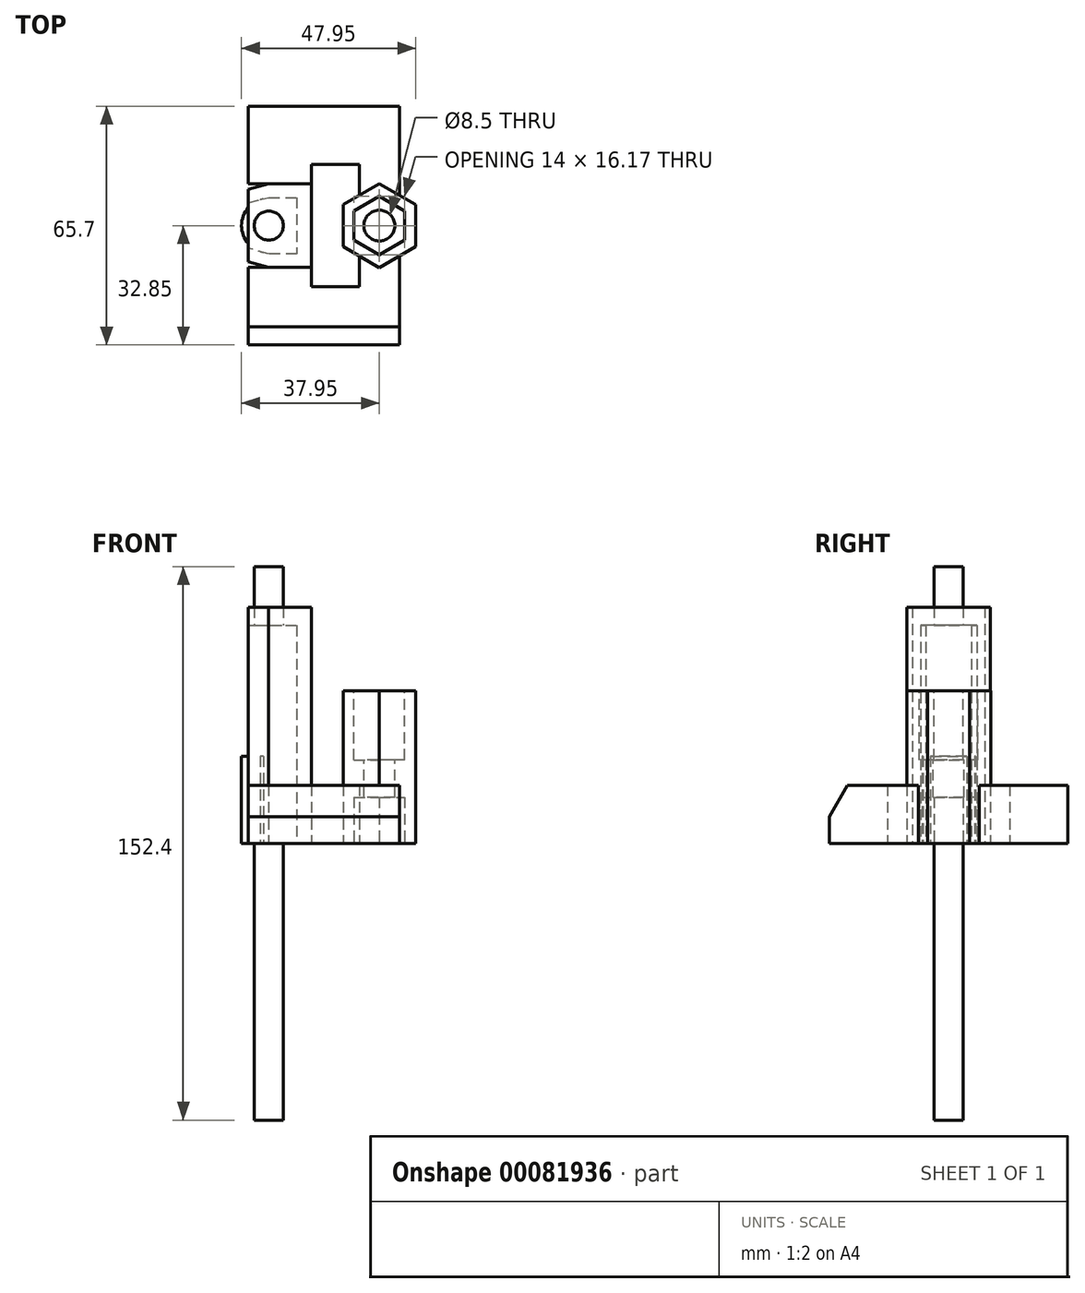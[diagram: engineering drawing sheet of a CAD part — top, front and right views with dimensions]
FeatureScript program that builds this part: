
annotation { "Feature Type Name" : "Feature", "Feature Type Description" : "" }
export const myFeature = defineFeature(function(context is Context, id is Id, definition is map)
    precondition{}
    {
        {
            var Q0;
            Q0=qCreatedBy(makeId("Top.planeOp"),FACE);
            var sketch = newSketch(context, id + "F0", { "sketchPlane" : qUnion([Q0])});
            skCircle(sketch, "E0", {"center": v(0, 0) * mm, "radius": 4 * mm});
            skSolve(sketch);
        }
        {
            var Q0;
            Q0 = qSketchRegion(id + "F0", true);
            extrude(context, id + "F1", {"entities" : qUnion([Q0]), "endBound" : BoundingType.SYMMETRIC, "depth" : 152.4 * mm});
        }
        {
            var Q0;
            Q0=qCreatedBy(makeId("Top.planeOp"),FACE);
            var sketch = newSketch(context, id + "F2", { "sketchPlane" : qUnion([Q0])});
            skLineSegment(sketch, "E1.bottom", {"start": v(0, 11.5) * mm, "end": v(11.7, 11.5) * mm});
            skLineSegment(sketch, "E1.top", {"start": v(0, -11.5) * mm, "end": v(11.7, -11.5) * mm});
            skLineSegment(sketch, "E1.left", {"start": v(-5.6, 10) * mm, "end": v(-5.6, -10) * mm});
            skLineSegment(sketch, "E1.right", {"start": v(11.7, 11.5) * mm, "end": v(11.7, -11.5) * mm});
            skLineSegment(sketch, "E2", {"start": v(0, 0) * mm, "end": v(-5.6, 0) * mm, "construction": true});
            skCircle(sketch, "E3", {"center": v(0, 0) * mm, "radius": 4 * mm, "construction": true});
            skLineSegment(sketch, "E4", {"start": v(-5.6, -10) * mm, "end": v(0, -11.5) * mm});
            skLineSegment(sketch, "E5", {"start": v(-5.6, 10) * mm, "end": v(0, 11.5) * mm});
            skLineSegment(sketch, "E6", {"start": v(0, -11.5) * mm, "end": v(-5.6, -11.5) * mm});
            skLineSegment(sketch, "E7", {"start": v(-5.6, -11.5) * mm, "end": v(-5.6, -32.85) * mm});
            skLineSegment(sketch, "E8", {"start": v(-5.6, -32.85) * mm, "end": v(35.95, -32.85) * mm});
            skLineSegment(sketch, "E9", {"start": v(35.95, -32.85) * mm, "end": v(35.95, -8.37) * mm});
            skLineSegment(sketch, "E10", {"start": v(35.95, -8.37) * mm, "end": v(24.95, -8.37) * mm});
            skLineSegment(sketch, "E11", {"start": v(24.95, -8.37) * mm, "end": v(24.95, -16.85) * mm});
            skLineSegment(sketch, "E12", {"start": v(24.95, -16.85) * mm, "end": v(11.7, -16.85) * mm});
            skLineSegment(sketch, "E13", {"start": v(11.7, -16.85) * mm, "end": v(11.7, -11.5) * mm});
            skLineSegment(sketch, "E14", {"start": v(0, 11.5) * mm, "end": v(-5.6, 11.5) * mm});
            skLineSegment(sketch, "E15", {"start": v(-5.6, 11.5) * mm, "end": v(-5.6, 32.85) * mm});
            skLineSegment(sketch, "E16", {"start": v(-5.6, 32.85) * mm, "end": v(35.95, 32.85) * mm});
            skLineSegment(sketch, "E17", {"start": v(35.95, 32.85) * mm, "end": v(35.95, 8.37) * mm});
            skLineSegment(sketch, "E18", {"start": v(35.95, 8.37) * mm, "end": v(24.95, 8.37) * mm});
            skLineSegment(sketch, "E19", {"start": v(24.95, 8.37) * mm, "end": v(24.95, 16.85) * mm});
            skLineSegment(sketch, "E20", {"start": v(24.95, 16.85) * mm, "end": v(11.7, 16.85) * mm});
            skLineSegment(sketch, "E21", {"start": v(11.7, 16.85) * mm, "end": v(11.7, 11.5) * mm});
            skCircle(sketch, "E22.cCircle", {"center": v(30.45, 0) * mm, "radius": 10 * mm, "construction": true});
            skLineSegment(sketch, "E22.0", {"start": v(40.45, 5.77) * mm, "end": v(40.45, -5.77) * mm});
            skLineSegment(sketch, "E22.1", {"start": v(40.45, -5.77) * mm, "end": v(30.45, -11.55) * mm});
            skLineSegment(sketch, "E22.2", {"start": v(30.45, -11.55) * mm, "end": v(20.45, -5.77) * mm});
            skLineSegment(sketch, "E22.3", {"start": v(20.45, -5.77) * mm, "end": v(20.45, 5.77) * mm});
            skLineSegment(sketch, "E22.4", {"start": v(20.45, 5.77) * mm, "end": v(30.45, 11.55) * mm});
            skLineSegment(sketch, "E22.5", {"start": v(30.45, 11.55) * mm, "end": v(40.45, 5.77) * mm});
            skPoint(sketch, "E22.0.midPoint", {"position": v(40.45, 0) * mm});
            skLineSegment(sketch, "E23", {"start": v(0, 0) * mm, "end": v(30.45, 0) * mm, "construction": true});
            skSolve(sketch);
        }
        {
            var Q0;
            Q0=qCreatedBy(makeId("Top.planeOp"),FACE);
            var sketch = newSketch(context, id + "F3", { "sketchPlane" : qUnion([Q0])});
            skCircle(sketch, "E24", {"center": v(0, 0) * mm, "radius": 4 * mm});
            skCircle(sketch, "E25", {"center": v(0, 0) * mm, "radius": 7.5 * mm});
            skSolve(sketch);
        }
        {
            var Q0;
            Q0=makeQuery(id+"F3.imprint","IMPRINT",FACE,{"disambiguationData":[TD([[makeQuery(id+"F3.imprint","IMPRINT",EDGE,{"derivedFrom":sQuery(id+"F3.wireOp",EDGE,"E24")}),-1.0]])]});
            extrude(context, id + "F4", {"entities" : qUnion([Q0]), "depth" : 24 * mm});
        }
        {
            var Q0;
            Q0=makeQuery(id+"F2.imprint","IMPRINT",FACE,{"disambiguationData":[TD([[makeQuery(id+"F2.imprint","IMPRINT",EDGE,{"derivedFrom":sQuery(id+"F2.wireOp",EDGE,"E1.bottom")}),-1.0]])]});
            extrude(context, id + "F5", {"entities" : qUnion([Q0]), "depth" : 65 * mm});
        }
        {
            var Q0;
            Q0=makeQuery(id+"F2.imprint","IMPRINT",FACE,{"disambiguationData":[TD([[makeQuery(id+"F2.imprint","IMPRINT",EDGE,{"derivedFrom":sQuery(id+"F2.wireOp",EDGE,"E1.top")}),-1.0]])]});
            var Q1;
            Q1=makeQuery(id+"F2.imprint","IMPRINT",FACE,{"disambiguationData":[TD([[makeQuery(id+"F2.imprint","IMPRINT",EDGE,{"derivedFrom":sQuery(id+"F2.wireOp",EDGE,"E1.bottom")}),1.0]])]});
            var Q2;
            {var subQ0=sQuery(id+"F2.wireOp",EDGE,"E18");Q2=makeQuery(id+"F2.imprint","IMPRINT",FACE,{"disambiguationData":[TD([[makeQuery(id+"F2.imprint","IMPRINT",EDGE,{"derivedFrom":subQ0}),-1.0]])]});}
            var Q3;
            {var subQ0=sQuery(id+"F2.wireOp",EDGE,"E10");Q3=makeQuery(id+"F2.imprint","IMPRINT",FACE,{"disambiguationData":[TD([[makeQuery(id+"F2.imprint","IMPRINT",EDGE,{"derivedFrom":subQ0}),1.0]])]});}
            extrude(context, id + "F6", {"entities" : qUnion([Q0, Q1, Q2, Q3]), "operationType" : NewBodyOperationType.ADD, "depth" : 16 * mm});
        }
        {
            var Q0;
            {var subQ1=sQuery(id+"F2.wireOp",EDGE,"E10");Q0=makeQuery(id+"F2.imprint","IMPRINT",FACE,{"disambiguationData":[TD([[makeQuery(id+"F2.imprint","IMPRINT",EDGE,{"derivedFrom":subQ1}),-1.0]])]});}
            var Q1;
            {var subQ0=sQuery(id+"F2.wireOp",EDGE,"E10");Q1=makeQuery(id+"F2.imprint","IMPRINT",FACE,{"disambiguationData":[TD([[makeQuery(id+"F2.imprint","IMPRINT",EDGE,{"derivedFrom":subQ0}),1.0]])]});}
            var Q2;
            {var subQ0=sQuery(id+"F2.wireOp",EDGE,"E18");Q2=makeQuery(id+"F2.imprint","IMPRINT",FACE,{"disambiguationData":[TD([[makeQuery(id+"F2.imprint","IMPRINT",EDGE,{"derivedFrom":subQ0}),-1.0]])]});}
            extrude(context, id + "F7", {"entities" : qUnion([Q0, Q1, Q2]), "operationType" : NewBodyOperationType.ADD, "depth" : 42 * mm});
        }
        {
            var Q0;
            Q0=makeQuery(id+"F7.opExtrude","CAP_FACE",FACE,{"disambiguationData":[OSD([sQuery(id+"F2.wireOp",EDGE,"E22.0"),sQuery(id+"F2.wireOp",EDGE,"E22.1"),sQuery(id+"F2.wireOp",EDGE,"E22.2"),sQuery(id+"F2.wireOp",EDGE,"E22.3"),sQuery(id+"F2.wireOp",EDGE,"E22.4"),sQuery(id+"F2.wireOp",EDGE,"E22.5")])],"isStart":false});
            var sketch = newSketch(context, id + "F8", { "sketchPlane" : qUnion([Q0])});
            skCircle(sketch, "E26.cCircle", {"center": v(30.45, 0) * mm, "radius": 7 * mm, "construction": true});
            skLineSegment(sketch, "E26.0", {"start": v(37.45, -4.04) * mm, "end": v(30.45, -8.08) * mm});
            skLineSegment(sketch, "E26.1", {"start": v(30.45, -8.08) * mm, "end": v(23.45, -4.04) * mm});
            skLineSegment(sketch, "E26.2", {"start": v(23.45, -4.04) * mm, "end": v(23.45, 4.04) * mm});
            skLineSegment(sketch, "E26.3", {"start": v(23.45, 4.04) * mm, "end": v(30.45, 8.08) * mm});
            skLineSegment(sketch, "E26.4", {"start": v(30.45, 8.08) * mm, "end": v(37.45, 4.04) * mm});
            skLineSegment(sketch, "E26.5", {"start": v(37.45, 4.04) * mm, "end": v(37.45, -4.04) * mm});
            skPoint(sketch, "E26.0.midPoint", {"position": v(33.95, -6.06) * mm});
            skSolve(sketch);
        }
        {
            var Q0;
            Q0 = qSketchRegion(id + "F8", true);
            extrude(context, id + "F9", {"entities" : qUnion([Q0]), "operationType" : NewBodyOperationType.REMOVE, "oppositeDirection" : true, "depth" : 19.05 * mm});
        }
        {
            var Q0;
            {var subQ1=sQuery(id+"F2.wireOp",EDGE,"E10");Q0=makeQuery(id+"F2.imprint","IMPRINT",FACE,{"disambiguationData":[TD([[makeQuery(id+"F2.imprint","IMPRINT",EDGE,{"derivedFrom":subQ1}),-1.0]])]});}
            var sketch = newSketch(context, id + "F10", { "sketchPlane" : qUnion([Q0])});
            skCircle(sketch, "E27.cCircle", {"center": v(30.45, 0) * mm, "radius": 7 * mm, "construction": true});
            skLineSegment(sketch, "E27.0", {"start": v(30.45, 8.08) * mm, "end": v(37.45, 4.04) * mm});
            skLineSegment(sketch, "E27.1", {"start": v(37.45, 4.04) * mm, "end": v(37.45, -4.04) * mm});
            skLineSegment(sketch, "E27.2", {"start": v(37.45, -4.04) * mm, "end": v(30.45, -8.08) * mm});
            skLineSegment(sketch, "E27.3", {"start": v(30.45, -8.08) * mm, "end": v(23.45, -4.04) * mm});
            skLineSegment(sketch, "E27.4", {"start": v(23.45, -4.04) * mm, "end": v(23.45, 4.04) * mm});
            skLineSegment(sketch, "E27.5", {"start": v(23.45, 4.04) * mm, "end": v(30.45, 8.08) * mm});
            skPoint(sketch, "E27.0.midPoint", {"position": v(33.95, 6.06) * mm});
            skSolve(sketch);
        }
        {
            var Q0;
            Q0 = qSketchRegion(id + "F10", true);
            extrude(context, id + "F11", {"entities" : qUnion([Q0]), "operationType" : NewBodyOperationType.REMOVE, "depth" : 12.7 * mm});
        }
        {
            var Q0;
            Q0=makeQuery(id+"F9.boolean.opBoolean","COPY",FACE,{"derivedFrom":makeQuery(id+"F9.opExtrude","CAP_FACE",FACE,{"disambiguationData":[OSD([sQuery(id+"F8.wireOp",EDGE,"E26.0"),sQuery(id+"F8.wireOp",EDGE,"E26.1"),sQuery(id+"F8.wireOp",EDGE,"E26.2"),sQuery(id+"F8.wireOp",EDGE,"E26.3"),sQuery(id+"F8.wireOp",EDGE,"E26.4"),sQuery(id+"F8.wireOp",EDGE,"E26.5")])],"isStart":false})});
            var sketch = newSketch(context, id + "F12", { "sketchPlane" : qUnion([Q0])});
            skCircle(sketch, "E28", {"center": v(30.45, 0) * mm, "radius": 4.25 * mm});
            skSolve(sketch);
        }
        {
            var Q0;
            Q0 = qSketchRegion(id + "F12", true);
            extrude(context, id + "F13", {"entities" : qUnion([Q0]), "operationType" : NewBodyOperationType.REMOVE, "endBound" : BoundingType.THROUGH_ALL, "oppositeDirection" : true, "depth" : 25.4 * mm});
        }
        {
            var Q0;
            Q0=makeQuery(id+"F6.opExtrude","CAP_EDGE",EDGE,{"disambiguationData":[OSD([sQuery(id+"F2.wireOp",EDGE,"E8")])],"isStart":false});
            chamfer(context, id + "F14", {"entities" : qUnion([Q0]), "chamferType" : ChamferType.OFFSET_ANGLE, "width" : 5 * mm, "oppositeDirection" : false, "angle" : 60 * degree, "tangentPropagation" : true});
        }
        {
            var Q0;
            {var subQ0=sQuery(id+"F2.wireOp",EDGE,"E1.top");var subQ1=sQuery(id+"F2.wireOp",EDGE,"E1.bottom");Q0=makeQuery(id+"F7.boolean.opBoolean","MERGE",FACE,{"derivedFrom":[makeQuery(id+"F6.boolean.opBoolean","MERGE",FACE,{"derivedFrom":[makeQuery(id+"F5.opExtrude","CAP_FACE",FACE,{"disambiguationData":[OSD([subQ1,subQ0,sQuery(id+"F2.wireOp",EDGE,"E1.left"),sQuery(id+"F2.wireOp",EDGE,"E1.right"),sQuery(id+"F2.wireOp",EDGE,"E4"),sQuery(id+"F2.wireOp",EDGE,"E5")])],"isStart":true}),makeQuery(id+"F6.opExtrude","CAP_FACE",FACE,{"disambiguationData":[OSD([subQ1,sQuery(id+"F2.wireOp",EDGE,"E14"),sQuery(id+"F2.wireOp",EDGE,"E15"),sQuery(id+"F2.wireOp",EDGE,"E16"),sQuery(id+"F2.wireOp",EDGE,"E17"),sQuery(id+"F2.wireOp",EDGE,"E18"),sQuery(id+"F2.wireOp",EDGE,"E19"),sQuery(id+"F2.wireOp",EDGE,"E20"),sQuery(id+"F2.wireOp",EDGE,"E21")])],"isStart":true}),makeQuery(id+"F6.opExtrude","CAP_FACE",FACE,{"disambiguationData":[OSD([subQ0,sQuery(id+"F2.wireOp",EDGE,"E6"),sQuery(id+"F2.wireOp",EDGE,"E7"),sQuery(id+"F2.wireOp",EDGE,"E8"),sQuery(id+"F2.wireOp",EDGE,"E9"),sQuery(id+"F2.wireOp",EDGE,"E10"),sQuery(id+"F2.wireOp",EDGE,"E11"),sQuery(id+"F2.wireOp",EDGE,"E12"),sQuery(id+"F2.wireOp",EDGE,"E13")])],"isStart":true})]}),makeQuery(id+"F7.opExtrude","CAP_FACE",FACE,{"disambiguationData":[OSD([sQuery(id+"F2.wireOp",EDGE,"E22.0"),sQuery(id+"F2.wireOp",EDGE,"E22.1"),sQuery(id+"F2.wireOp",EDGE,"E22.2"),sQuery(id+"F2.wireOp",EDGE,"E22.3"),sQuery(id+"F2.wireOp",EDGE,"E22.4"),sQuery(id+"F2.wireOp",EDGE,"E22.5")])],"isStart":true})]});}
            var sketch = newSketch(context, id + "F15", { "sketchPlane" : qUnion([Q0])});
            skLineSegment(sketch, "E29", {"start": v(-5.6, -6.25) * mm, "end": v(0, -7.75) * mm});
            skLineSegment(sketch, "E30", {"start": v(0, -7.75) * mm, "end": v(7.7, -7.75) * mm});
            skLineSegment(sketch, "E31", {"start": v(7.7, -7.75) * mm, "end": v(7.7, 7.75) * mm});
            skLineSegment(sketch, "E32", {"start": v(7.7, 7.75) * mm, "end": v(0, 7.75) * mm});
            skLineSegment(sketch, "E33", {"start": v(0, 7.75) * mm, "end": v(-5.6, 6.25) * mm});
            skLineSegment(sketch, "E34", {"start": v(-5.6, 6.25) * mm, "end": v(-5.6, -6.25) * mm});
            skLineSegment(sketch, "E35", {"start": v(7.7, 0) * mm, "end": v(11.7, 0) * mm, "construction": true});
            skSolve(sketch);
        }
        {
            var Q0;
            Q0 = qSketchRegion(id + "F15", true);
            extrude(context, id + "F16", {"entities" : qUnion([Q0]), "operationType" : NewBodyOperationType.REMOVE, "oppositeDirection" : true, "depth" : 60 * mm});
        }
    });
